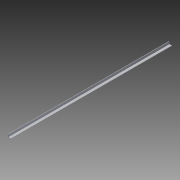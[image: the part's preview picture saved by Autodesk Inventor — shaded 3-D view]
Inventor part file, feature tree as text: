
AUTODESK INVENTOR PART (.ipt)
format: ipt  version: 2013 (Build 170138000, 138)  size: 73,728 bytes
history: native  units: in
note: dims shown in document units (in); Inventor stores cm internally (conversion verified against a paired STEP export)
features: extrude x1, sketch x1
ambient origin geometry x8: Origin, YZ Plane, XZ Plane, XY Plane, X Axis, Y Axis, Z Axis, Center Point
bodies: Solid1 (feature_tree)
feature tree (2):
  extrude  "Extrusion1"  Depth=0.0625in
  sketch  "Sketch1"  dims[d0=0.5in d1=0.0625in d2=0.5in d3=0.0625in d4=28.5in d5=0.0in]
